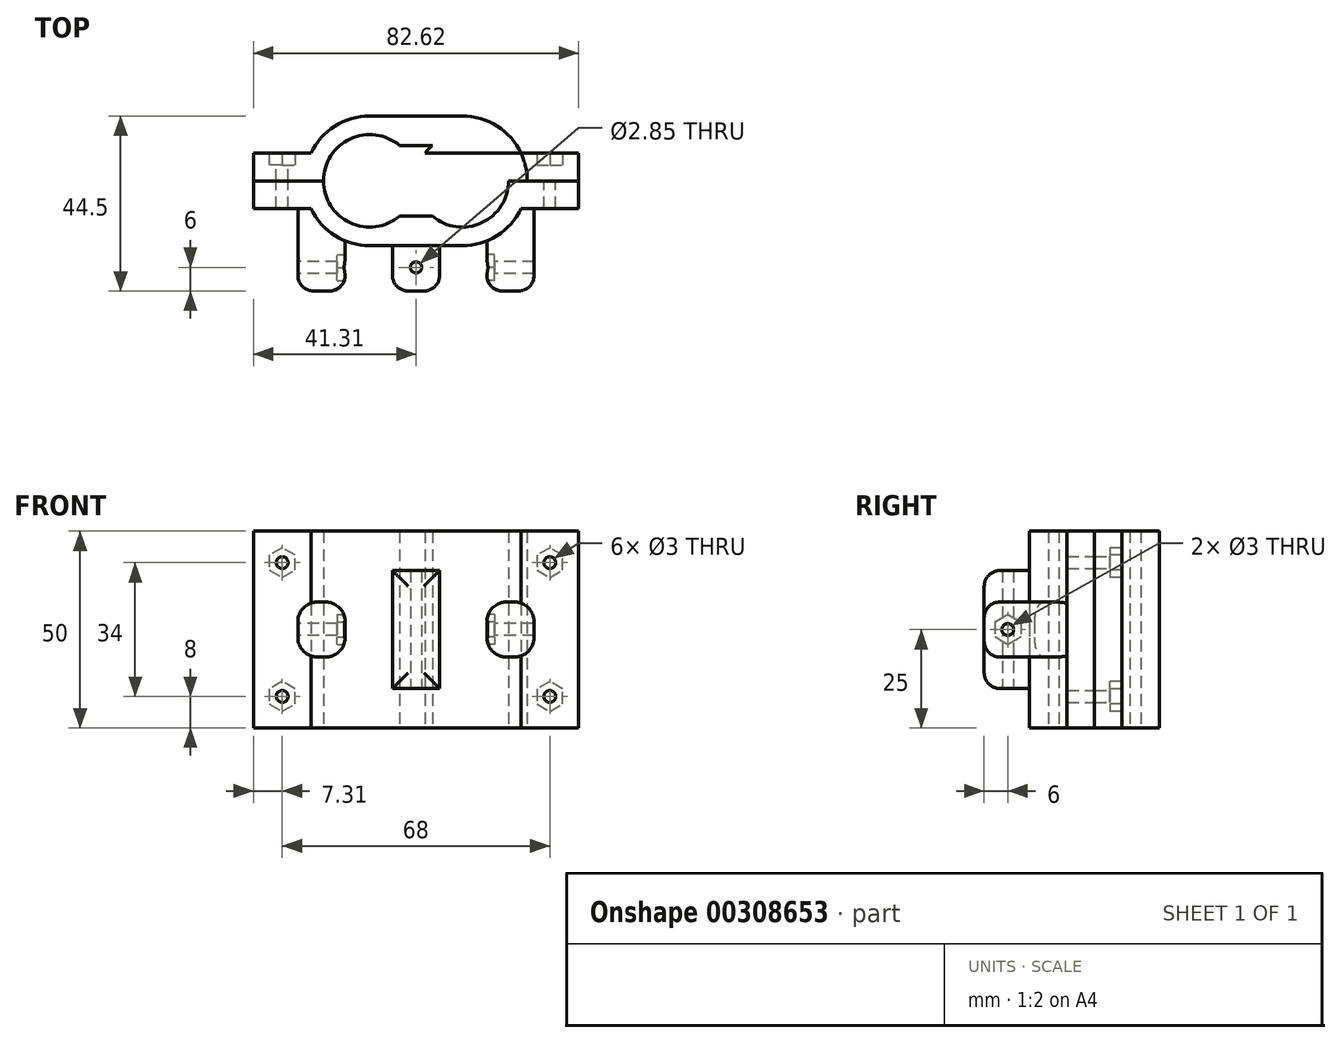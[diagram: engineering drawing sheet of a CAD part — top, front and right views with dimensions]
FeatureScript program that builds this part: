
annotation { "Feature Type Name" : "Feature", "Feature Type Description" : "" }
export const myFeature = defineFeature(function(context is Context, id is Id, definition is map)
    precondition{}
    {
        {
            var Q0;
            Q0=qCreatedBy(makeId("Top.planeOp"),FACE);
            var sketch = newSketch(context, id + "F0", { "sketchPlane" : qUnion([Q0])});
            skCircle(sketch, "E0", {"center": v(-11.75, 0) * mm, "radius": 11.75 * mm});
            skCircle(sketch, "E1.MirrorC", {"center": v(11.75, 0) * mm, "radius": 11.75 * mm});
            skArc(sketch, "E2", {"start": v(0, 11.58) * mm, "mid": v(-28.25, 0) * mm, "end": v(0, -11.58) * mm});
            skArc(sketch, "E3.MirrorC", {"start": v(0, 11.58) * mm, "mid": v(28.25, 0) * mm, "end": v(0, -11.58) * mm});
            skLineSegment(sketch, "E4", {"start": v(0, 0) * mm, "end": v(-28.25, 0) * mm});
            skLineSegment(sketch, "E5.MirrorCS", {"start": v(0, 0) * mm, "end": v(28.25, 0) * mm});
            skLineSegment(sketch, "E6.0", {"start": v(0, 7) * mm, "end": v(-26.7, 7) * mm});
            skLineSegment(sketch, "E7", {"start": v(-41.3, 7) * mm, "end": v(-41.3, 0) * mm});
            skLineSegment(sketch, "E8", {"start": v(-41.3, 0) * mm, "end": v(0, 0) * mm});
            skLineSegment(sketch, "E9.MirrorCS", {"start": v(0, 7) * mm, "end": v(26.7, 7) * mm});
            skLineSegment(sketch, "E10.MirrorCS", {"start": v(41.3, 0) * mm, "end": v(0, 0) * mm});
            skLineSegment(sketch, "E11.MirrorCS", {"start": v(41.3, 7) * mm, "end": v(41.3, 0) * mm});
            skLineSegment(sketch, "E12.MirrorCS", {"start": v(26.7, 7) * mm, "end": v(41.3, 7) * mm});
            skLineSegment(sketch, "E13", {"start": v(-26.7, 7) * mm, "end": v(-41.3, 7) * mm});
            skLineSegment(sketch, "E14", {"start": v(-34, 7) * mm, "end": v(-34, 0) * mm});
            skLineSegment(sketch, "E15.0", {"start": v(-35.5, 7) * mm, "end": v(-35.5, 0) * mm});
            skLineSegment(sketch, "E16.0", {"start": v(-32.5, 7) * mm, "end": v(-32.5, 0) * mm});
            skLineSegment(sketch, "E17.MirrorCS", {"start": v(32.5, 7) * mm, "end": v(32.5, 0) * mm});
            skLineSegment(sketch, "E18.MirrorCS", {"start": v(34, 7) * mm, "end": v(34, 0) * mm});
            skLineSegment(sketch, "E19.MirrorCS", {"start": v(35.5, 7) * mm, "end": v(35.5, 0) * mm});
            skPoint(sketch, "E20.orphan", {"position": v(0, 23.5) * mm});
            skLineSegment(sketch, "E21", {"start": v(-4.2, 9) * mm, "end": v(4.2, 9) * mm});
            skLineSegment(sketch, "E22.MirrorCS", {"start": v(-4.2, -9) * mm, "end": v(4.2, -9) * mm});
            skLineSegment(sketch, "E23.MirrorCS", {"start": v(26.7, -7) * mm, "end": v(41.3, -7) * mm});
            skLineSegment(sketch, "E24.MirrorCS", {"start": v(32.5, -7) * mm, "end": v(32.5, 0) * mm});
            skLineSegment(sketch, "E25.MirrorCS", {"start": v(34, -7) * mm, "end": v(34, 0) * mm});
            skLineSegment(sketch, "E26.MirrorCS", {"start": v(35.5, -7) * mm, "end": v(35.5, 0) * mm});
            skLineSegment(sketch, "E27.MirrorCS", {"start": v(41.3, -7) * mm, "end": v(41.3, 0) * mm});
            skLineSegment(sketch, "E28.MirrorCS", {"start": v(-26.7, -7) * mm, "end": v(-41.3, -7) * mm});
            skLineSegment(sketch, "E29.MirrorCS", {"start": v(-41.3, -7) * mm, "end": v(-41.3, 0) * mm});
            skLineSegment(sketch, "E30.MirrorCS", {"start": v(-35.5, -7) * mm, "end": v(-35.5, 0) * mm});
            skLineSegment(sketch, "E31.MirrorCS", {"start": v(-34, -7) * mm, "end": v(-34, 0) * mm});
            skLineSegment(sketch, "E32.MirrorCS", {"start": v(-32.5, -7) * mm, "end": v(-32.5, 0) * mm});
            skLineSegment(sketch, "E33", {"start": v(11.75, -16.5) * mm, "end": v(-11.75, -16.5) * mm});
            skLineSegment(sketch, "E34", {"start": v(11.75, 16.5) * mm, "end": v(-11.75, 16.5) * mm});
            skLineSegment(sketch, "E35", {"start": v(30, -7) * mm, "end": v(30, -28) * mm});
            skLineSegment(sketch, "E36.0", {"start": v(18, -15.27) * mm, "end": v(18, -28) * mm});
            skLineSegment(sketch, "E37", {"start": v(18, -28) * mm, "end": v(30, -28) * mm});
            skLineSegment(sketch, "E38.MirrorCS", {"start": v(-18, -15.27) * mm, "end": v(-18, -28) * mm});
            skLineSegment(sketch, "E39.MirrorCS", {"start": v(-18, -28) * mm, "end": v(-30, -28) * mm});
            skLineSegment(sketch, "E40.MirrorCS", {"start": v(-30, -7) * mm, "end": v(-30, -28) * mm});
            skLineSegment(sketch, "E41", {"start": v(0, -16.5) * mm, "end": v(0, -28) * mm});
            skPoint(sketch, "E41.endSnap0", {"position": v(0, -16.5) * mm});
            skLineSegment(sketch, "E42", {"start": v(-6, -28) * mm, "end": v(6, -28) * mm});
            skPoint(sketch, "E43.orphan", {"position": v(0, -30.01) * mm});
            skLineSegment(sketch, "E44.0", {"start": v(-6, -16.5) * mm, "end": v(-6, -28) * mm});
            skLineSegment(sketch, "E45.0", {"start": v(6, -16.5) * mm, "end": v(6, -28) * mm});
            skCircle(sketch, "E46", {"center": v(0, -22) * mm, "radius": 1.43 * mm});
            skSolve(sketch);
        }
        {
            var Q0;
            {var subQ4=sQuery(id+"F0.wireOp",EDGE,"E21");Q0=makeQuery(id+"F0.imprint","IMPRINT",FACE,{"disambiguationData":[TD([[makeQuery(id+"F0.imprint","IMPRINT",EDGE,{"derivedFrom":subQ4}),1.0]])]});}
            var Q1;
            {var subQ4=sQuery(id+"F0.wireOp",EDGE,"E21");Q1=makeQuery(id+"F0.imprint","IMPRINT",FACE,{"disambiguationData":[TD([[makeQuery(id+"F0.imprint","IMPRINT",EDGE,{"derivedFrom":subQ4}),1.0]])]});}
            var Q2;
            {var subQ0=sQuery(id+"F0.wireOp",EDGE,"E11.MirrorCS");Q2=makeQuery(id+"F0.imprint","IMPRINT",FACE,{"disambiguationData":[TD([[makeQuery(id+"F0.imprint","IMPRINT",EDGE,{"derivedFrom":subQ0}),-1.0]])]});}
            var Q3;
            {var subQ0=sQuery(id+"F0.wireOp",EDGE,"E7");Q3=makeQuery(id+"F0.imprint","IMPRINT",FACE,{"disambiguationData":[TD([[makeQuery(id+"F0.imprint","IMPRINT",EDGE,{"derivedFrom":subQ0}),1.0]])]});}
            var Q4;
            {var subQ0=sQuery(id+"F0.wireOp",EDGE,"E14");Q4=makeQuery(id+"F0.imprint","IMPRINT",FACE,{"disambiguationData":[TD([[makeQuery(id+"F0.imprint","IMPRINT",EDGE,{"derivedFrom":subQ0}),-1.0]])]});}
            var Q5;
            {var subQ0=sQuery(id+"F0.wireOp",EDGE,"E14");Q5=makeQuery(id+"F0.imprint","IMPRINT",FACE,{"disambiguationData":[TD([[makeQuery(id+"F0.imprint","IMPRINT",EDGE,{"derivedFrom":subQ0}),1.0]])]});}
            var Q6;
            {var subQ0=sQuery(id+"F0.wireOp",EDGE,"E16.0");Q6=makeQuery(id+"F0.imprint","IMPRINT",FACE,{"disambiguationData":[TD([[makeQuery(id+"F0.imprint","IMPRINT",EDGE,{"derivedFrom":subQ0}),1.0]])]});}
            var Q7;
            {var subQ0=sQuery(id+"F0.wireOp",EDGE,"E17.MirrorCS");Q7=makeQuery(id+"F0.imprint","IMPRINT",FACE,{"disambiguationData":[TD([[makeQuery(id+"F0.imprint","IMPRINT",EDGE,{"derivedFrom":subQ0}),1.0]])]});}
            var Q8;
            {var subQ4=sQuery(id+"F0.wireOp",EDGE,"E17.MirrorCS");Q8=makeQuery(id+"F0.imprint","IMPRINT",FACE,{"disambiguationData":[TD([[makeQuery(id+"F0.imprint","IMPRINT",EDGE,{"derivedFrom":subQ4}),-1.0]])]});}
            var Q9;
            {var subQ0=sQuery(id+"F0.wireOp",EDGE,"E18.MirrorCS");Q9=makeQuery(id+"F0.imprint","IMPRINT",FACE,{"disambiguationData":[TD([[makeQuery(id+"F0.imprint","IMPRINT",EDGE,{"derivedFrom":subQ0}),1.0]])]});}
            var Q10;
            {var subQ0=sQuery(id+"F0.wireOp",EDGE,"E6.0");var subQ1=sQuery(id+"F0.wireOp",EDGE,"E0");var subQ2=makeQuery(id+"F0.imprint","INTERSECT",VERTEX,{"disambiguationData":[OD(1.0)],"derivedFrom":[subQ1,subQ0]});Q10=makeQuery(id+"F0.imprint","IMPRINT",FACE,{"disambiguationData":[TD([[makeQuery(id+"F0.imprint","IMPRINT",EDGE,{"disambiguationData":[TD([[subQ2,-1.0]])],"derivedFrom":subQ1}),-1.0]])]});}
            var Q11;
            {var subQ0=sQuery(id+"F0.wireOp",EDGE,"E9.MirrorCS");var subQ1=sQuery(id+"F0.wireOp",EDGE,"E1.MirrorC");var subQ2=makeQuery(id+"F0.imprint","INTERSECT",VERTEX,{"disambiguationData":[OD(1.0)],"derivedFrom":[subQ1,subQ0]});Q11=makeQuery(id+"F0.imprint","IMPRINT",FACE,{"disambiguationData":[TD([[makeQuery(id+"F0.imprint","IMPRINT",EDGE,{"disambiguationData":[TD([[subQ2,-1.0]])],"derivedFrom":subQ1}),1.0]])]});}
            var Q12;
            {var subQ4=sQuery(id+"F0.wireOp",EDGE,"E21");Q12=makeQuery(id+"F0.imprint","IMPRINT",FACE,{"disambiguationData":[TD([[makeQuery(id+"F0.imprint","IMPRINT",EDGE,{"derivedFrom":subQ4}),1.0]])]});}
            var Q13;
            {var subQ4=sQuery(id+"F0.wireOp",EDGE,"E21");Q13=makeQuery(id+"F0.imprint","IMPRINT",FACE,{"disambiguationData":[TD([[makeQuery(id+"F0.imprint","IMPRINT",EDGE,{"derivedFrom":subQ4}),1.0]])]});}
            var Q14;
            {var subQ3=sQuery(id+"F0.wireOp",EDGE,"E34");Q14=makeQuery(id+"F0.imprint","IMPRINT",FACE,{"disambiguationData":[TD([[makeQuery(id+"F0.imprint","IMPRINT",EDGE,{"derivedFrom":subQ3}),1.0]])]});}
            extrude(context, id + "F1", {"entities" : qUnion([Q0, Q1, Q2, Q3, Q4, Q5, Q6, Q7, Q8, Q9, Q10, Q11, Q12, Q13, Q14]), "depth" : 50 * mm});
        }
        {
            var Q0;
            {var subQ0=sQuery(id+"F0.wireOp",EDGE,"E29.MirrorCS");Q0=makeQuery(id+"F0.imprint","IMPRINT",FACE,{"disambiguationData":[TD([[makeQuery(id+"F0.imprint","IMPRINT",EDGE,{"derivedFrom":subQ0}),-1.0]])]});}
            var Q1;
            {var subQ2=sQuery(id+"F0.wireOp",EDGE,"E30.MirrorCS");Q1=makeQuery(id+"F0.imprint","IMPRINT",FACE,{"disambiguationData":[TD([[makeQuery(id+"F0.imprint","IMPRINT",EDGE,{"derivedFrom":subQ2}),-1.0]])]});}
            var Q2;
            {var subQ0=sQuery(id+"F0.wireOp",EDGE,"E31.MirrorCS");Q2=makeQuery(id+"F0.imprint","IMPRINT",FACE,{"disambiguationData":[TD([[makeQuery(id+"F0.imprint","IMPRINT",EDGE,{"derivedFrom":subQ0}),-1.0]])]});}
            var Q3;
            {var subQ5=sQuery(id+"F0.wireOp",EDGE,"E32.MirrorCS");Q3=makeQuery(id+"F0.imprint","IMPRINT",FACE,{"disambiguationData":[TD([[makeQuery(id+"F0.imprint","IMPRINT",EDGE,{"derivedFrom":subQ5}),-1.0]])]});}
            var Q4;
            {var subQ4=sQuery(id+"F0.wireOp",EDGE,"E22.MirrorCS");Q4=makeQuery(id+"F0.imprint","IMPRINT",FACE,{"disambiguationData":[TD([[makeQuery(id+"F0.imprint","IMPRINT",EDGE,{"derivedFrom":subQ4}),-1.0]])]});}
            var Q5;
            {var subQ5=sQuery(id+"F0.wireOp",EDGE,"E24.MirrorCS");Q5=makeQuery(id+"F0.imprint","IMPRINT",FACE,{"disambiguationData":[TD([[makeQuery(id+"F0.imprint","IMPRINT",EDGE,{"derivedFrom":subQ5}),1.0]])]});}
            var Q6;
            {var subQ0=sQuery(id+"F0.wireOp",EDGE,"E24.MirrorCS");Q6=makeQuery(id+"F0.imprint","IMPRINT",FACE,{"disambiguationData":[TD([[makeQuery(id+"F0.imprint","IMPRINT",EDGE,{"derivedFrom":subQ0}),-1.0]])]});}
            var Q7;
            {var subQ0=sQuery(id+"F0.wireOp",EDGE,"E25.MirrorCS");Q7=makeQuery(id+"F0.imprint","IMPRINT",FACE,{"disambiguationData":[TD([[makeQuery(id+"F0.imprint","IMPRINT",EDGE,{"derivedFrom":subQ0}),-1.0]])]});}
            var Q8;
            {var subQ2=sQuery(id+"F0.wireOp",EDGE,"E26.MirrorCS");Q8=makeQuery(id+"F0.imprint","IMPRINT",FACE,{"disambiguationData":[TD([[makeQuery(id+"F0.imprint","IMPRINT",EDGE,{"derivedFrom":subQ2}),-1.0]])]});}
            var Q9;
            {var subQ3=sQuery(id+"F0.wireOp",EDGE,"E33");Q9=makeQuery(id+"F0.imprint","IMPRINT",FACE,{"disambiguationData":[TD([[makeQuery(id+"F0.imprint","IMPRINT",EDGE,{"derivedFrom":subQ3}),-1.0]])]});}
            extrude(context, id + "F2", {"entities" : qUnion([Q0, Q1, Q2, Q3, Q4, Q5, Q6, Q7, Q8, Q9]), "depth" : 50 * mm});
        }
        {
            var Q0;
            {var subQ0=sQuery(id+"F0.wireOp",EDGE,"E14");Q0=makeQuery(id+"F0.imprint","IMPRINT",FACE,{"disambiguationData":[TD([[makeQuery(id+"F0.imprint","IMPRINT",EDGE,{"derivedFrom":subQ0}),-1.0]])]});}
            var Q1;
            {var subQ2=sQuery(id+"F0.wireOp",EDGE,"E30.MirrorCS");Q1=makeQuery(id+"F0.imprint","IMPRINT",FACE,{"disambiguationData":[TD([[makeQuery(id+"F0.imprint","IMPRINT",EDGE,{"derivedFrom":subQ2}),-1.0]])]});}
            var Q2;
            Q2=sQuery(id+"F0.wireOp",EDGE,"E14");
            revolve(context, id + "F3", {"entities" : qUnion([Q0, Q1]), "axis" : qUnion([Q2]), "revolveType" : RevolveType.FULL});
        }
        {
            var Q0;
            {var subQ0=sQuery(id+"F0.wireOp",EDGE,"E18.MirrorCS");Q0=makeQuery(id+"F0.imprint","IMPRINT",FACE,{"disambiguationData":[TD([[makeQuery(id+"F0.imprint","IMPRINT",EDGE,{"derivedFrom":subQ0}),1.0]])]});}
            var Q1;
            {var subQ0=sQuery(id+"F0.wireOp",EDGE,"E25.MirrorCS");Q1=makeQuery(id+"F0.imprint","IMPRINT",FACE,{"disambiguationData":[TD([[makeQuery(id+"F0.imprint","IMPRINT",EDGE,{"derivedFrom":subQ0}),-1.0]])]});}
            var Q2;
            Q2=sQuery(id+"F0.wireOp",EDGE,"E18.MirrorCS");
            revolve(context, id + "F4", {"entities" : qUnion([Q0, Q1]), "axis" : qUnion([Q2]), "revolveType" : RevolveType.FULL});
        }
        {
            var Q0;
            {var subQ0=sQuery(id+"F0.wireOp",EDGE,"E18.MirrorCS");Q0=makeQuery(id+"F0.imprint","IMPRINT",FACE,{"disambiguationData":[TD([[makeQuery(id+"F0.imprint","IMPRINT",EDGE,{"derivedFrom":subQ0}),1.0]])]});}
            var Q1;
            {var subQ0=sQuery(id+"F0.wireOp",EDGE,"E25.MirrorCS");Q1=makeQuery(id+"F0.imprint","IMPRINT",FACE,{"disambiguationData":[TD([[makeQuery(id+"F0.imprint","IMPRINT",EDGE,{"derivedFrom":subQ0}),-1.0]])]});}
            var Q2;
            Q2=sQuery(id+"F0.wireOp",EDGE,"E18.MirrorCS");
            revolve(context, id + "F5", {"entities" : qUnion([Q0, Q1]), "axis" : qUnion([Q2]), "revolveType" : RevolveType.FULL});
        }
        {
            var Q0;
            {var subQ0=sQuery(id+"F0.wireOp",EDGE,"E14");Q0=makeQuery(id+"F0.imprint","IMPRINT",FACE,{"disambiguationData":[TD([[makeQuery(id+"F0.imprint","IMPRINT",EDGE,{"derivedFrom":subQ0}),1.0]])]});}
            var Q1;
            {var subQ0=sQuery(id+"F0.wireOp",EDGE,"E31.MirrorCS");Q1=makeQuery(id+"F0.imprint","IMPRINT",FACE,{"disambiguationData":[TD([[makeQuery(id+"F0.imprint","IMPRINT",EDGE,{"derivedFrom":subQ0}),-1.0]])]});}
            var Q2;
            Q2=sQuery(id+"F0.wireOp",EDGE,"E14");
            revolve(context, id + "F6", {"entities" : qUnion([Q0, Q1]), "axis" : qUnion([Q2]), "revolveType" : RevolveType.FULL});
        }
        {
            var Q0;
            Q0=makeQuery(id+"F3.opRevolve","SWEPT_BODY",BODY,{"disambiguationData":[OSD([sQuery(id+"F0.wireOp",EDGE,"E8"),sQuery(id+"F0.wireOp",EDGE,"E13"),sQuery(id+"F0.wireOp",EDGE,"E14"),sQuery(id+"F0.wireOp",EDGE,"E15.0")])]});
            var Q1;
            Q1=makeQuery(id+"F4.opRevolve","SWEPT_BODY",BODY,{"disambiguationData":[OSD([sQuery(id+"F0.wireOp",EDGE,"E10.MirrorCS"),sQuery(id+"F0.wireOp",EDGE,"E12.MirrorCS"),sQuery(id+"F0.wireOp",EDGE,"E18.MirrorCS"),sQuery(id+"F0.wireOp",EDGE,"E19.MirrorCS")])]});
            transform(context, id + "F7", {"entities" : qUnion([Q0, Q1]), "transformType" : TransformType.TRANSLATION_3D, "dx" : 0 * mm, "dy" : 0 * mm, "dz" : 42 * mm, "makeCopy" : false});
        }
        {
            var Q0;
            Q0=makeQuery(id+"F6.opRevolve","SWEPT_BODY",BODY,{"disambiguationData":[OSD([sQuery(id+"F0.wireOp",EDGE,"E8"),sQuery(id+"F0.wireOp",EDGE,"E13"),sQuery(id+"F0.wireOp",EDGE,"E14"),sQuery(id+"F0.wireOp",EDGE,"E16.0")])]});
            var Q1;
            Q1=makeQuery(id+"F5.opRevolve","SWEPT_BODY",BODY,{"disambiguationData":[OSD([sQuery(id+"F0.wireOp",EDGE,"E10.MirrorCS"),sQuery(id+"F0.wireOp",EDGE,"E12.MirrorCS"),sQuery(id+"F0.wireOp",EDGE,"E18.MirrorCS"),sQuery(id+"F0.wireOp",EDGE,"E19.MirrorCS")])]});
            transform(context, id + "F8", {"entities" : qUnion([Q0, Q1]), "transformType" : TransformType.TRANSLATION_3D, "dx" : 0 * mm, "dy" : 0 * mm, "dz" : 8 * mm, "makeCopy" : false});
        }
        {
            var Q0;
            Q0=qCreatedBy(makeId("Front.planeOp"),FACE);
            var sketch = newSketch(context, id + "F9", { "sketchPlane" : qUnion([Q0])});
            skCircle(sketch, "E47.cCircle", {"center": v(34, 42) * mm, "radius": 3.28 * mm, "construction": true});
            skLineSegment(sketch, "E47.0", {"start": v(37.27, 43.9) * mm, "end": v(37.27, 40.1) * mm});
            skLineSegment(sketch, "E47.1", {"start": v(37.27, 40.1) * mm, "end": v(34, 38.22) * mm});
            skLineSegment(sketch, "E47.2", {"start": v(34, 38.22) * mm, "end": v(30.73, 40.1) * mm});
            skLineSegment(sketch, "E47.3", {"start": v(30.73, 40.1) * mm, "end": v(30.73, 43.9) * mm});
            skLineSegment(sketch, "E47.4", {"start": v(30.72, 43.9) * mm, "end": v(34, 45.78) * mm});
            skLineSegment(sketch, "E47.5", {"start": v(34, 45.78) * mm, "end": v(37.27, 43.9) * mm});
            skPoint(sketch, "E47.0.midPoint", {"position": v(37.27, 42) * mm});
            skCircle(sketch, "E48.cCircle", {"center": v(34, 8) * mm, "radius": 3.28 * mm, "construction": true});
            skLineSegment(sketch, "E48.0", {"start": v(37.28, 9.9) * mm, "end": v(37.28, 6.1) * mm});
            skLineSegment(sketch, "E48.1", {"start": v(37.28, 6.1) * mm, "end": v(34, 4.22) * mm});
            skLineSegment(sketch, "E48.2", {"start": v(34, 4.22) * mm, "end": v(30.73, 6.1) * mm});
            skLineSegment(sketch, "E48.3", {"start": v(30.73, 6.1) * mm, "end": v(30.73, 9.9) * mm});
            skLineSegment(sketch, "E48.4", {"start": v(30.73, 9.9) * mm, "end": v(34, 11.78) * mm});
            skLineSegment(sketch, "E48.5", {"start": v(34, 11.78) * mm, "end": v(37.28, 9.9) * mm});
            skPoint(sketch, "E48.0.midPoint", {"position": v(37.28, 8) * mm});
            skCircle(sketch, "E49.MirrorC", {"center": v(-34, 42) * mm, "radius": 3.28 * mm, "construction": true});
            skLineSegment(sketch, "E50.MirrorCS", {"start": v(-30.72, 43.9) * mm, "end": v(-34, 45.78) * mm});
            skLineSegment(sketch, "E51.MirrorCS", {"start": v(-37.27, 43.9) * mm, "end": v(-37.27, 40.1) * mm});
            skLineSegment(sketch, "E52.MirrorCS", {"start": v(-34, 38.22) * mm, "end": v(-30.73, 40.1) * mm});
            skLineSegment(sketch, "E53.MirrorCS", {"start": v(-34, 45.78) * mm, "end": v(-37.27, 43.9) * mm});
            skLineSegment(sketch, "E54.MirrorCS", {"start": v(-37.27, 40.1) * mm, "end": v(-34, 38.22) * mm});
            skPoint(sketch, "E55.MirrorP", {"position": v(-37.27, 42) * mm});
            skLineSegment(sketch, "E56.MirrorCS", {"start": v(-30.73, 40.1) * mm, "end": v(-30.73, 43.9) * mm});
            skLineSegment(sketch, "E57.MirrorCS", {"start": v(-30.73, 9.9) * mm, "end": v(-34, 11.78) * mm});
            skLineSegment(sketch, "E58.MirrorCS", {"start": v(-30.73, 6.1) * mm, "end": v(-30.73, 9.9) * mm});
            skLineSegment(sketch, "E59.MirrorCS", {"start": v(-34, 11.78) * mm, "end": v(-37.28, 9.9) * mm});
            skLineSegment(sketch, "E60.MirrorCS", {"start": v(-37.28, 6.1) * mm, "end": v(-34, 4.22) * mm});
            skLineSegment(sketch, "E61.MirrorCS", {"start": v(-37.28, 9.9) * mm, "end": v(-37.28, 6.1) * mm});
            skLineSegment(sketch, "E62.MirrorCS", {"start": v(-34, 4.22) * mm, "end": v(-30.73, 6.1) * mm});
            skPoint(sketch, "E63.MirrorP", {"position": v(-37.28, 8) * mm});
            skCircle(sketch, "E64.MirrorC", {"center": v(-34, 8) * mm, "radius": 3.28 * mm, "construction": true});
            skLineSegment(sketch, "E65.left", {"start": v(-35.75, 32.5) * mm, "end": v(-35.75, 17.5) * mm});
            skLineSegment(sketch, "E65.right", {"start": v(-32.25, 32.5) * mm, "end": v(-32.25, 17.5) * mm});
            skLineSegment(sketch, "E66.MirrorCS", {"start": v(32.25, 32.5) * mm, "end": v(32.25, 17.5) * mm});
            skLineSegment(sketch, "E67.MirrorCS", {"start": v(35.75, 32.5) * mm, "end": v(35.75, 17.5) * mm});
            skArc(sketch, "E68", {"start": v(-32.25, 32.5) * mm, "mid": v(-34, 34.25) * mm, "end": v(-35.75, 32.5) * mm});
            skArc(sketch, "E69", {"start": v(-35.75, 17.5) * mm, "mid": v(-34, 15.75) * mm, "end": v(-32.25, 17.5) * mm});
            skArc(sketch, "E70.MirrorCS", {"start": v(35.75, 17.5) * mm, "mid": v(34, 15.75) * mm, "end": v(32.25, 17.5) * mm});
            skArc(sketch, "E71.MirrorCS", {"start": v(32.25, 32.5) * mm, "mid": v(34, 34.25) * mm, "end": v(35.75, 32.5) * mm});
            skPoint(sketch, "E72.orphan", {"position": v(35.75, 32.5) * mm});
            skPoint(sketch, "E73.MirrorCS.end.orphan", {"position": v(32.25, 32.5) * mm});
            skPoint(sketch, "E74.orphan", {"position": v(32.25, 17.5) * mm});
            skPoint(sketch, "E75.MirrorCS.start.orphan", {"position": v(35.75, 17.5) * mm});
            skLineSegment(sketch, "E76.bottom", {"start": v(32.25, 28.5) * mm, "end": v(35.75, 28.5) * mm});
            skLineSegment(sketch, "E76.top", {"start": v(32.25, 21.5) * mm, "end": v(35.75, 21.5) * mm});
            skLineSegment(sketch, "E76.left", {"start": v(32.25, 28.5) * mm, "end": v(32.25, 21.5) * mm});
            skLineSegment(sketch, "E77.MirrorCS", {"start": v(-32.25, 28.5) * mm, "end": v(-35.75, 28.5) * mm});
            skLineSegment(sketch, "E78.MirrorCS", {"start": v(-32.25, 21.5) * mm, "end": v(-35.75, 21.5) * mm});
            skSolve(sketch);
        }
        {
            var Q0;
            Q0=makeQuery(id+"F9.imprint","IMPRINT",FACE,{"disambiguationData":[TD([[makeQuery(id+"F9.imprint","IMPRINT",EDGE,{"derivedFrom":sQuery(id+"F9.wireOp",EDGE,"E47.0")}),-1.0]])]});
            var Q1;
            Q1=makeQuery(id+"F9.imprint","IMPRINT",FACE,{"disambiguationData":[TD([[makeQuery(id+"F9.imprint","IMPRINT",EDGE,{"derivedFrom":sQuery(id+"F9.wireOp",EDGE,"E48.0")}),-1.0]])]});
            var Q2;
            Q2=makeQuery(id+"F9.imprint","IMPRINT",FACE,{"disambiguationData":[TD([[makeQuery(id+"F9.imprint","IMPRINT",EDGE,{"derivedFrom":sQuery(id+"F9.wireOp",EDGE,"E57.MirrorCS")}),1.0]])]});
            var Q3;
            Q3=makeQuery(id+"F9.imprint","IMPRINT",FACE,{"disambiguationData":[TD([[makeQuery(id+"F9.imprint","IMPRINT",EDGE,{"derivedFrom":sQuery(id+"F9.wireOp",EDGE,"E50.MirrorCS")}),1.0]])]});
            extrude(context, id + "F10", {"entities" : qUnion([Q0, Q1, Q2, Q3]), "operationType" : NewBodyOperationType.REMOVE, "oppositeDirection" : true, "depth" : 25 * mm, "hasSecondDirection" : true, "secondDirectionOppositeDirection" : true, "secondDirectionDepth" : 4 * mm});
        }
        {
            var Q0;
            Q0=qCreatedBy(makeId("Right.planeOp"),FACE);
            var sketch = newSketch(context, id + "F11", { "sketchPlane" : qUnion([Q0])});
            skCircle(sketch, "E79.cCircle", {"center": v(-22, 25) * mm, "radius": 3.28 * mm, "construction": true});
            skLineSegment(sketch, "E79.0", {"start": v(-18.72, 26.9) * mm, "end": v(-18.72, 23.1) * mm});
            skLineSegment(sketch, "E79.1", {"start": v(-18.72, 23.1) * mm, "end": v(-22, 21.22) * mm});
            skLineSegment(sketch, "E79.2", {"start": v(-22, 21.22) * mm, "end": v(-25.27, 23.1) * mm});
            skLineSegment(sketch, "E79.3", {"start": v(-25.27, 23.1) * mm, "end": v(-25.27, 26.9) * mm});
            skLineSegment(sketch, "E79.4", {"start": v(-25.27, 26.9) * mm, "end": v(-22, 28.78) * mm});
            skLineSegment(sketch, "E79.5", {"start": v(-22, 28.78) * mm, "end": v(-18.72, 26.9) * mm});
            skPoint(sketch, "E79.0.midPoint", {"position": v(-18.72, 25) * mm});
            skCircle(sketch, "E80", {"center": v(-22, 25) * mm, "radius": 1.5 * mm});
            skSolve(sketch);
        }
        {
            var Q0;
            Q0=makeQuery(id+"F4.opRevolve","SWEPT_BODY",BODY,{"disambiguationData":[OSD([sQuery(id+"F0.wireOp",EDGE,"E12.MirrorCS"),sQuery(id+"F0.wireOp",EDGE,"E18.MirrorCS"),sQuery(id+"F0.wireOp",EDGE,"E19.MirrorCS"),sQuery(id+"F0.wireOp",EDGE,"E23.MirrorCS"),sQuery(id+"F0.wireOp",EDGE,"E25.MirrorCS"),sQuery(id+"F0.wireOp",EDGE,"E26.MirrorCS")])]});
            var Q1;
            Q1=makeQuery(id+"FH7VoqV1SiyAWcH_5.opRevolve","SWEPT_BODY",BODY,{"disambiguationData":[OSD([sQuery(id+"F0.wireOp",EDGE,"2DyHF6Rm-Xbol-s4WK-JNq4-YZTDFXXxcwj8"),sQuery(id+"F0.wireOp",EDGE,"oBKz860q-5wVE-mCj7-cvw1-Y41J6N8gphqz"),sQuery(id+"F0.wireOp",EDGE,"1929efcb-dddd-4ffd-ba50-d8c2afb98746.0"),sQuery(id+"F0.wireOp",EDGE,"afe7083f-1648-42ab-bf03-8e5b259d3504.0")])]});
            var Q2;
            Q2=makeQuery(id+"F5.opRevolve","SWEPT_BODY",BODY,{"disambiguationData":[OSD([sQuery(id+"F0.wireOp",EDGE,"E12.MirrorCS"),sQuery(id+"F0.wireOp",EDGE,"E18.MirrorCS"),sQuery(id+"F0.wireOp",EDGE,"E19.MirrorCS"),sQuery(id+"F0.wireOp",EDGE,"E23.MirrorCS"),sQuery(id+"F0.wireOp",EDGE,"E25.MirrorCS"),sQuery(id+"F0.wireOp",EDGE,"E26.MirrorCS")])]});
            var Q3;
            Q3=makeQuery(id+"F0jYo1nIoFjdefQ_6.opRevolve","SWEPT_BODY",BODY,{"disambiguationData":[OSD([sQuery(id+"F0.wireOp",EDGE,"a2ce7271-9f92-45c3-972d-1d20a637b6140.MirrorCS"),sQuery(id+"F0.wireOp",EDGE,"77dbbf6e-9c1c-4305-9500-1d0fac70a6f00.MirrorCS"),sQuery(id+"F0.wireOp",EDGE,"d47600f9-f3fd-4ec0-93dc-5c5839c0d2410.MirrorCS"),sQuery(id+"F0.wireOp",EDGE,"7367f09b-41cc-4809-a2d5-d795fc4837c70.MirrorCS")])]});
            var Q4;
            Q4=makeQuery(id+"F3.opRevolve","SWEPT_BODY",BODY,{"disambiguationData":[OSD([sQuery(id+"F0.wireOp",EDGE,"E13"),sQuery(id+"F0.wireOp",EDGE,"E14"),sQuery(id+"F0.wireOp",EDGE,"E15.0"),sQuery(id+"F0.wireOp",EDGE,"E28.MirrorCS"),sQuery(id+"F0.wireOp",EDGE,"E30.MirrorCS"),sQuery(id+"F0.wireOp",EDGE,"E31.MirrorCS")])]});
            var Q5;
            Q5=makeQuery(id+"F6.opRevolve","SWEPT_BODY",BODY,{"disambiguationData":[OSD([sQuery(id+"F0.wireOp",EDGE,"E13"),sQuery(id+"F0.wireOp",EDGE,"E14"),sQuery(id+"F0.wireOp",EDGE,"E16.0"),sQuery(id+"F0.wireOp",EDGE,"E28.MirrorCS"),sQuery(id+"F0.wireOp",EDGE,"E31.MirrorCS"),sQuery(id+"F0.wireOp",EDGE,"E32.MirrorCS")])]});
            var Q6;
            Q6=makeQuery(id+"F1.opExtrude","SWEPT_BODY",BODY,{"disambiguationData":[OSD([sQuery(id+"F0.wireOp",EDGE,"E0"),sQuery(id+"F0.wireOp",EDGE,"E1.MirrorC"),sQuery(id+"F0.wireOp",EDGE,"E2"),sQuery(id+"F0.wireOp",EDGE,"E3.MirrorC"),sQuery(id+"F0.wireOp",EDGE,"E7"),sQuery(id+"F0.wireOp",EDGE,"E8"),sQuery(id+"F0.wireOp",EDGE,"E10.MirrorCS"),sQuery(id+"F0.wireOp",EDGE,"E11.MirrorCS"),sQuery(id+"F0.wireOp",EDGE,"E12.MirrorCS"),sQuery(id+"F0.wireOp",EDGE,"E13"),sQuery(id+"F0.wireOp",EDGE,"E21"),sQuery(id+"F0.wireOp",EDGE,"E22.MirrorCS")])]});
            var Q7;
            Q7=makeQuery(id+"F2.opExtrude","SWEPT_BODY",BODY,{"disambiguationData":[OSD([sQuery(id+"F0.wireOp",EDGE,"E0"),sQuery(id+"F0.wireOp",EDGE,"E1.MirrorC"),sQuery(id+"F0.wireOp",EDGE,"E2"),sQuery(id+"F0.wireOp",EDGE,"E3.MirrorC"),sQuery(id+"F0.wireOp",EDGE,"E8"),sQuery(id+"F0.wireOp",EDGE,"E10.MirrorCS"),sQuery(id+"F0.wireOp",EDGE,"E22.MirrorCS"),sQuery(id+"F0.wireOp",EDGE,"E23.MirrorCS"),sQuery(id+"F0.wireOp",EDGE,"E27.MirrorCS"),sQuery(id+"F0.wireOp",EDGE,"E28.MirrorCS"),sQuery(id+"F0.wireOp",EDGE,"E29.MirrorCS")])]});
            var Q8;
            Q8=makeQuery(id+"FpWEQBjlzGKV5Kr_2.opExtrude","SWEPT_BODY",BODY,{"disambiguationData":[OSD([sQuery(id+"F0.wireOp",EDGE,"E3.MirrorC"),sQuery(id+"F0.wireOp",EDGE,"E12.MirrorCS"),sQuery(id+"F0.wireOp",EDGE,"BltonAJx-7N8s-ZKYv-OiXr-XgwGRrNKy8pZ"),sQuery(id+"F0.wireOp",EDGE,"2DyHF6Rm-Xbol-s4WK-JNq4-YZTDFXXxcwj8"),sQuery(id+"F0.wireOp",EDGE,"oBKz860q-5wVE-mCj7-cvw1-Y41J6N8gphqz"),sQuery(id+"F0.wireOp",EDGE,"DwHz4Wtu-yHvy-4auB-OP2u-JiOUzi7Gbt5m")])]});
            var Q9;
            Q9=makeQuery(id+"FpWEQBjlzGKV5Kr_2.opExtrude","SWEPT_BODY",BODY,{"disambiguationData":[OSD([sQuery(id+"F0.wireOp",EDGE,"E2"),sQuery(id+"F0.wireOp",EDGE,"E13"),sQuery(id+"F0.wireOp",EDGE,"3eea5a1e-ca78-410a-b10a-bee36d02c2840.MirrorCS"),sQuery(id+"F0.wireOp",EDGE,"d47600f9-f3fd-4ec0-93dc-5c5839c0d2410.MirrorCS"),sQuery(id+"F0.wireOp",EDGE,"7367f09b-41cc-4809-a2d5-d795fc4837c70.MirrorCS"),sQuery(id+"F0.wireOp",EDGE,"4d77f2e1-2c14-4bb0-9c13-9b87fb32e19e0.MirrorCS")])]});
            booleanBodies(context, id + "F12", {"operationType" : BooleanOperationType.SUBTRACTION, "tools" : qUnion([Q0, Q1, Q2, Q3, Q4, Q5]), "targets" : qUnion([Q6, Q7, Q8, Q9])});
        }
        {
            var Q0;
            {var subQ0=sQuery(id+"F0.wireOp",EDGE,"E38.MirrorCS");Q0=makeQuery(id+"F0.imprint","IMPRINT",FACE,{"disambiguationData":[TD([[makeQuery(id+"F0.imprint","IMPRINT",EDGE,{"derivedFrom":subQ0}),-1.0]])]});}
            var Q1;
            {var subQ0=sQuery(id+"F0.wireOp",EDGE,"E35");Q1=makeQuery(id+"F0.imprint","IMPRINT",FACE,{"disambiguationData":[TD([[makeQuery(id+"F0.imprint","IMPRINT",EDGE,{"derivedFrom":subQ0}),-1.0]])]});}
            extrude(context, id + "F13", {"entities" : qUnion([Q0, Q1]), "operationType" : NewBodyOperationType.ADD, "depth" : 32 * mm, "hasSecondDirection" : true, "secondDirectionOppositeDirection" : false, "secondDirectionDepth" : 18 * mm});
        }
        {
            var Q0;
            Q0=makeQuery(id+"F11.imprint","IMPRINT",FACE,{"disambiguationData":[TD([[makeQuery(id+"F11.imprint","IMPRINT",EDGE,{"derivedFrom":sQuery(id+"F11.wireOp",EDGE,"E80")}),1.0]])]});
            extrude(context, id + "F14", {"entities" : qUnion([Q0]), "operationType" : NewBodyOperationType.REMOVE, "depth" : 35 * mm, "hasSecondDirection" : true, "secondDirectionOppositeDirection" : true, "secondDirectionDepth" : 35 * mm});
        }
        {
            var Q0;
            Q0=makeQuery(id+"F13.opExtrude","SWEPT_EDGE",EDGE,{"disambiguationData":[OSD([sQuery(id+"F0.wireOp",EDGE,"E35"),sQuery(id+"F0.wireOp",EDGE,"E37")])]});
            var Q1;
            Q1=makeQuery(id+"F13.opExtrude","CAP_EDGE",EDGE,{"disambiguationData":[OSD([sQuery(id+"F0.wireOp",EDGE,"E37")])],"isStart":true});
            var Q2;
            Q2=makeQuery(id+"F13.opExtrude","CAP_EDGE",EDGE,{"disambiguationData":[OSD([sQuery(id+"F0.wireOp",EDGE,"E37")])],"isStart":false});
            var Q3;
            Q3=makeQuery(id+"F13.opExtrude","SWEPT_FACE",FACE,{"disambiguationData":[OSD([sQuery(id+"F0.wireOp",EDGE,"E37")])]});
            var Q4;
            Q4=makeQuery(id+"F13.opExtrude","SWEPT_EDGE",EDGE,{"disambiguationData":[OSD([sQuery(id+"F0.wireOp",EDGE,"E38.MirrorCS"),sQuery(id+"F0.wireOp",EDGE,"E39.MirrorCS")])]});
            var Q5;
            Q5=makeQuery(id+"F13.opExtrude","CAP_EDGE",EDGE,{"disambiguationData":[OSD([sQuery(id+"F0.wireOp",EDGE,"E39.MirrorCS")])],"isStart":false});
            var Q6;
            Q6=makeQuery(id+"F13.opExtrude","SWEPT_EDGE",EDGE,{"disambiguationData":[OSD([sQuery(id+"F0.wireOp",EDGE,"E39.MirrorCS"),sQuery(id+"F0.wireOp",EDGE,"E40.MirrorCS")])]});
            var Q7;
            Q7=makeQuery(id+"F13.opExtrude","CAP_EDGE",EDGE,{"disambiguationData":[OSD([sQuery(id+"F0.wireOp",EDGE,"E39.MirrorCS")])],"isStart":true});
            fillet(context, id + "F15", {"entities" : qUnion([Q0, Q1, Q2, Q3, Q4, Q5, Q6, Q7]), "radius" : 4 * mm, "tangentPropagation" : true, "allowEdgeOverflow" : false});
        }
        {
            var Q0;
            {var subQ0=sQuery(id+"F0.wireOp",EDGE,"E41");Q0=makeQuery(id+"F0.imprint","IMPRINT",FACE,{"disambiguationData":[TD([[makeQuery(id+"F0.imprint","IMPRINT",EDGE,{"derivedFrom":subQ0}),-1.0]])]});}
            var Q1;
            {var subQ0=sQuery(id+"F0.wireOp",EDGE,"E41");Q1=makeQuery(id+"F0.imprint","IMPRINT",FACE,{"disambiguationData":[TD([[makeQuery(id+"F0.imprint","IMPRINT",EDGE,{"derivedFrom":subQ0}),1.0]])]});}
            extrude(context, id + "F16", {"entities" : qUnion([Q0, Q1]), "operationType" : NewBodyOperationType.ADD, "depth" : 40 * mm, "hasSecondDirection" : true, "secondDirectionOppositeDirection" : false, "secondDirectionDepth" : 10 * mm});
        }
        {
            var Q0;
            Q0=makeQuery(id+"F16.opExtrude","SWEPT_EDGE",EDGE,{"disambiguationData":[OSD([sQuery(id+"F0.wireOp",EDGE,"E42"),sQuery(id+"F0.wireOp",EDGE,"E45.0")])]});
            var Q1;
            Q1=makeQuery(id+"F16.opExtrude","CAP_EDGE",EDGE,{"disambiguationData":[OSD([sQuery(id+"F0.wireOp",EDGE,"E42")])],"isStart":false});
            var Q2;
            Q2=makeQuery(id+"F16.opExtrude","SWEPT_EDGE",EDGE,{"disambiguationData":[OSD([sQuery(id+"F0.wireOp",EDGE,"E42"),sQuery(id+"F0.wireOp",EDGE,"E44.0")])]});
            var Q3;
            Q3=makeQuery(id+"F16.opExtrude","CAP_EDGE",EDGE,{"disambiguationData":[OSD([sQuery(id+"F0.wireOp",EDGE,"E42")])],"isStart":true});
            fillet(context, id + "F17", {"entities" : qUnion([Q0, Q1, Q2, Q3]), "radius" : 4 * mm, "tangentPropagation" : true, "allowEdgeOverflow" : false});
        }
        {
            var Q0;
            Q0=makeQuery(id+"F13.opExtrude","CAP_EDGE",EDGE,{"disambiguationData":[OSD([sQuery(id+"F0.wireOp",EDGE,"E35")])],"isStart":true});
            var Q1;
            Q1=makeQuery(id+"F13.opExtrude","CAP_EDGE",EDGE,{"disambiguationData":[OSD([sQuery(id+"F0.wireOp",EDGE,"E35")])],"isStart":false});
            var Q2;
            Q2=makeQuery(id+"F13.opExtrude","CAP_EDGE",EDGE,{"disambiguationData":[OSD([sQuery(id+"F0.wireOp",EDGE,"E36.0")])],"isStart":false});
            var Q3;
            Q3=makeQuery(id+"F13.opExtrude","CAP_EDGE",EDGE,{"disambiguationData":[OSD([sQuery(id+"F0.wireOp",EDGE,"E36.0")])],"isStart":true});
            var Q4;
            Q4=makeQuery(id+"F13.opExtrude","CAP_EDGE",EDGE,{"disambiguationData":[OSD([sQuery(id+"F0.wireOp",EDGE,"E38.MirrorCS")])],"isStart":false});
            var Q5;
            Q5=makeQuery(id+"F13.opExtrude","CAP_EDGE",EDGE,{"disambiguationData":[OSD([sQuery(id+"F0.wireOp",EDGE,"E38.MirrorCS")])],"isStart":true});
            var Q6;
            Q6=makeQuery(id+"F13.opExtrude","CAP_EDGE",EDGE,{"disambiguationData":[OSD([sQuery(id+"F0.wireOp",EDGE,"E40.MirrorCS")])],"isStart":false});
            var Q7;
            Q7=makeQuery(id+"F13.opExtrude","CAP_EDGE",EDGE,{"disambiguationData":[OSD([sQuery(id+"F0.wireOp",EDGE,"E40.MirrorCS")])],"isStart":true});
            fillet(context, id + "F18", {"entities" : qUnion([Q0, Q1, Q2, Q3, Q4, Q5, Q6, Q7]), "radius" : 5 * mm, "tangentPropagation" : true, "allowEdgeOverflow" : false});
        }
        {
            var Q0;
            Q0=makeQuery(id+"F11.imprint","IMPRINT",FACE,{"disambiguationData":[TD([[makeQuery(id+"F11.imprint","IMPRINT",EDGE,{"derivedFrom":sQuery(id+"F11.wireOp",EDGE,"E79.0")}),-1.0]])]});
            extrude(context, id + "F19", {"entities" : qUnion([Q0]), "operationType" : NewBodyOperationType.REMOVE, "oppositeDirection" : true, "depth" : 20 * mm, "hasSecondDirection" : true, "secondDirectionOppositeDirection" : true, "secondDirectionDepth" : 10 * mm});
        }
        {
            var Q0;
            Q0=makeQuery(id+"F11.imprint","IMPRINT",FACE,{"disambiguationData":[TD([[makeQuery(id+"F11.imprint","IMPRINT",EDGE,{"derivedFrom":sQuery(id+"F11.wireOp",EDGE,"E79.0")}),-1.0]])]});
            extrude(context, id + "F20", {"entities" : qUnion([Q0]), "operationType" : NewBodyOperationType.REMOVE, "depth" : 20 * mm, "hasSecondDirection" : true, "secondDirectionOppositeDirection" : false, "secondDirectionDepth" : 10 * mm});
        }
    });
